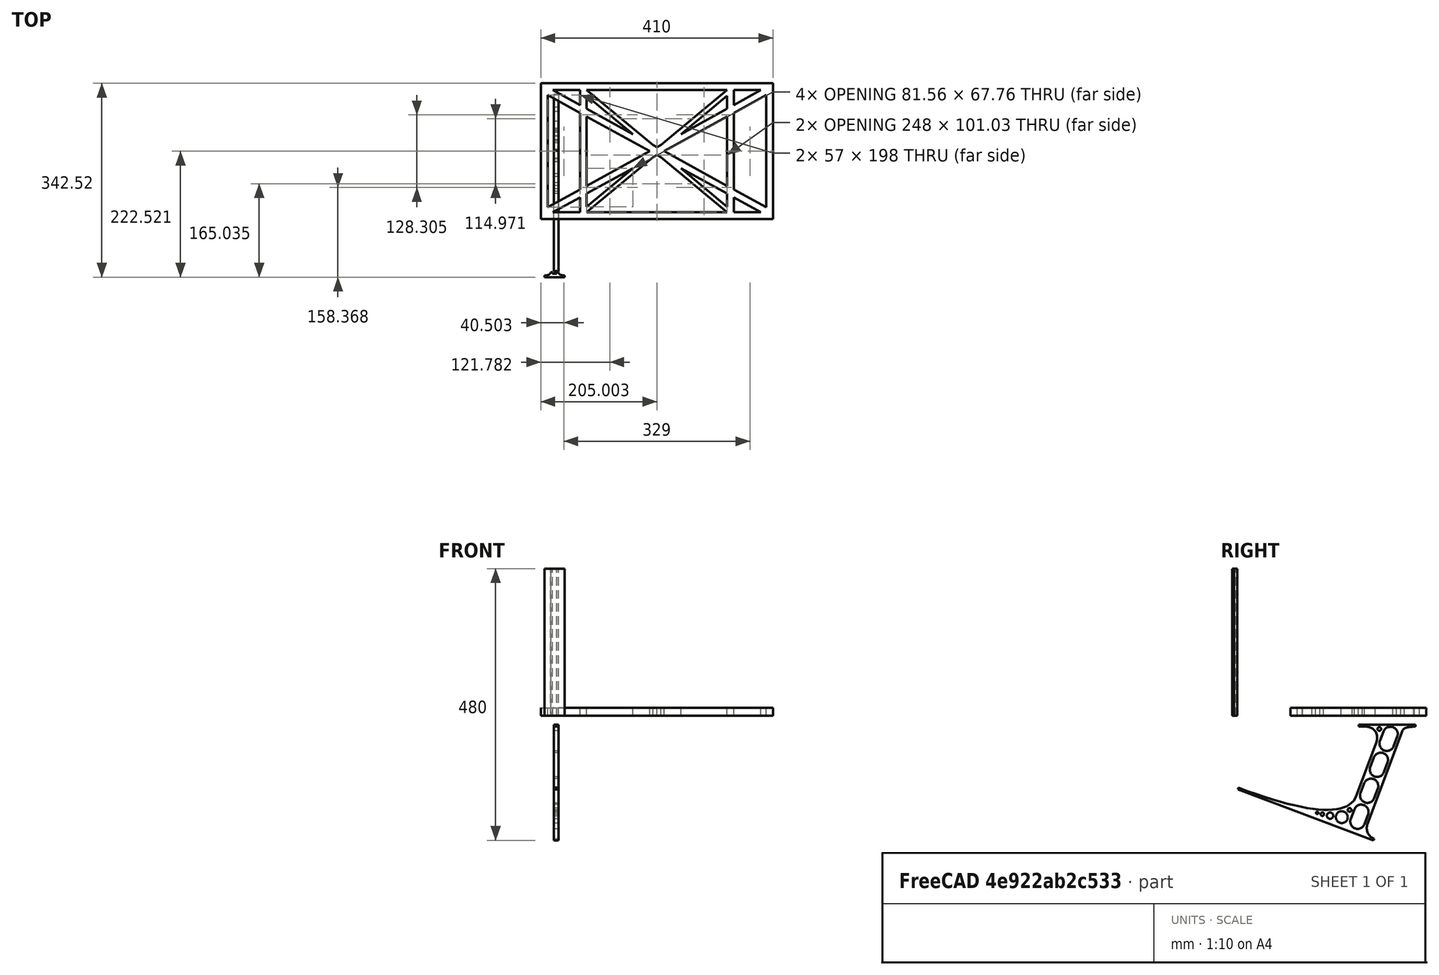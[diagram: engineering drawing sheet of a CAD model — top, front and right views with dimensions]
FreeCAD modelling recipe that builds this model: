
FCSTD DOCUMENT  (FreeCAD 0.19R0.19.2)
Label: laptopStand052
License: All rights reserved
LicenseURL: http://en.wikipedia.org/wiki/All_rights_reserved
objects: Sketcher::SketchObject×3, Part::Extrusion×3
note: 6 computed .brp shape members not serialized (recipe doc carries the construction recipe); baked Part::Feature solids carry a one-line shape summary decoded from their .brp

FEATURE [Sketcher::SketchObject] Sketch
  FullyConstrained = true
  sketch-geometry (90):
    g0: LineSegment StartX=-22.9272 StartY=136.221 StartZ=0 EndX=387.073 EndY=136.221 EndZ=0
    g1: LineSegment StartX=-22.9272 StartY=-103.779 StartZ=0 EndX=387.073 EndY=-103.779 EndZ=0
    g2: LineSegment StartX=375.073 StartY=115.221 StartZ=0 EndX=318.073 EndY=83.9235 EndZ=0
    g3: LineSegment StartX=-10.9272 StartY=-82.7794 StartZ=0 EndX=46.0728 EndY=-51.4823 EndZ=0
    g4: LineSegment StartX=-1.92719 StartY=124.221 StartZ=0 EndX=46.0728 EndY=97.8651 EndZ=0
    g5: LineSegment StartX=366.073 StartY=-91.7794 StartZ=0 EndX=318.073 EndY=-65.424 EndZ=0
    g6: LineSegment StartX=-10.9272 StartY=115.221 StartZ=0 EndX=-10.9272 EndY=-82.7794 EndZ=0
    g7: LineSegment StartX=375.073 StartY=-82.7794 StartZ=0 EndX=375.073 EndY=115.221 EndZ=0
    g8: LineSegment StartX=-1.92719 StartY=-91.7794 StartZ=0 EndX=46.0728 EndY=-91.7794 EndZ=0
    g9: LineSegment StartX=318.073 StartY=124.221 StartZ=0 EndX=366.073 EndY=124.221 EndZ=0
    g10: LineSegment StartX=306.073 StartY=-81.8102 StartZ=0 EndX=224.513 EndY=-14.0532 EndZ=0
    g11: LineSegment StartX=58.0728 StartY=114.251 StartZ=0 EndX=139.632 EndY=46.4944 EndZ=0
    g12: LineSegment StartX=306.073 StartY=124.221 StartZ=0 EndX=189.124 EndY=27.0628 EndZ=0
    g13: LineSegment StartX=58.0728 StartY=-91.7794 StartZ=0 EndX=175.022 EndY=5.37834 EndZ=0
    g14: LineSegment StartX=46.0728 StartY=124.221 StartZ=0 EndX=46.0728 EndY=97.8651 EndZ=0
    g15: LineSegment StartX=58.0728 StartY=-81.8102 StartZ=0 EndX=58.0728 EndY=-58.8351 EndZ=0
    g16: LineSegment StartX=318.073 StartY=124.221 StartZ=0 EndX=318.073 EndY=97.8651 EndZ=0
    g17: LineSegment StartX=306.073 StartY=114.251 StartZ=0 EndX=306.073 EndY=91.2763 EndZ=0
    g18: LineSegment StartX=224.513 StartY=46.4944 StartZ=0 EndX=306.073 EndY=114.251 EndZ=0
    g19: LineSegment StartX=175.022 StartY=27.0628 StartZ=0 EndX=58.0728 EndY=124.221 EndZ=0
    g20: LineSegment StartX=169.377 StartY=16.2206 StartZ=0 EndX=58.0728 EndY=77.3346 EndZ=0
    g21: LineSegment StartX=139.632 StartY=-14.0532 StartZ=0 EndX=58.0728 EndY=-81.8102 EndZ=0
    g22: LineSegment StartX=194.768 StartY=16.2206 StartZ=0 EndX=306.073 EndY=-44.8935 EndZ=0
    g23: LineSegment StartX=224.513 StartY=46.4944 StartZ=0 EndX=306.073 EndY=91.2763 EndZ=0
    g24: LineSegment StartX=139.632 StartY=-14.0532 StartZ=0 EndX=58.0728 EndY=-58.8351 EndZ=0
    g25: LineSegment StartX=189.124 StartY=5.37834 StartZ=0 EndX=306.073 EndY=-91.7794 EndZ=0
    g26: LineSegment StartX=306.073 StartY=77.3346 StartZ=0 EndX=306.073 EndY=-44.8935 EndZ=0
    g27: LineSegment StartX=318.073 StartY=83.9235 StartZ=0 EndX=318.073 EndY=-51.4823 EndZ=0
    g28: LineSegment StartX=318.073 StartY=97.8651 StartZ=0 EndX=366.073 EndY=124.221 EndZ=0
    g29: LineSegment StartX=306.073 StartY=77.3346 StartZ=0 EndX=194.768 EndY=16.2206 EndZ=0
    g30: LineSegment StartX=306.073 StartY=-58.8351 StartZ=0 EndX=224.513 EndY=-14.0532 EndZ=0
    g31: LineSegment StartX=306.073 StartY=-58.8351 StartZ=0 EndX=306.073 EndY=-81.8102 EndZ=0
    g32: LineSegment StartX=318.073 StartY=-51.4823 StartZ=0 EndX=375.073 EndY=-82.7794 EndZ=0
    g33: LineSegment StartX=318.073 StartY=-65.424 StartZ=0 EndX=318.073 EndY=-91.7794 EndZ=0
    g34: LineSegment StartX=318.073 StartY=-91.7794 StartZ=0 EndX=366.073 EndY=-91.7794 EndZ=0
    g35: LineSegment StartX=58.0728 StartY=-44.8935 StartZ=0 EndX=58.0728 EndY=77.3346 EndZ=0
    g36: LineSegment StartX=46.0728 StartY=-65.424 StartZ=0 EndX=-1.92719 EndY=-91.7794 EndZ=0
    g37: LineSegment StartX=46.0728 StartY=-65.424 StartZ=0 EndX=46.0728 EndY=-91.7794 EndZ=0
    g38: LineSegment StartX=58.0728 StartY=-44.8935 StartZ=0 EndX=169.377 EndY=16.2206 EndZ=0
    g39: LineSegment StartX=58.0728 StartY=91.2763 StartZ=0 EndX=58.0728 EndY=114.251 EndZ=0
    g40: LineSegment StartX=46.0728 StartY=83.9235 StartZ=0 EndX=46.0728 EndY=-51.4823 EndZ=0
    g41: LineSegment StartX=46.0728 StartY=124.221 StartZ=0 EndX=-1.92719 EndY=124.221 EndZ=0
    g42: LineSegment StartX=58.0728 StartY=91.2763 StartZ=0 EndX=139.632 EndY=46.4944 EndZ=0
    g43: LineSegment StartX=46.0728 StartY=83.9235 StartZ=0 EndX=-10.9272 EndY=115.221 EndZ=0
    g44: LineSegment StartX=-22.9272 StartY=136.221 StartZ=0 EndX=-42.9272 EndY=136.221 EndZ=0
    g45: LineSegment StartX=387.073 StartY=136.221 StartZ=0 EndX=407.073 EndY=136.221 EndZ=0
    g46: LineSegment StartX=-42.9272 StartY=136.221 StartZ=0 EndX=-42.9272 EndY=-103.779 EndZ=0
    g47: LineSegment StartX=-22.9272 StartY=-103.779 StartZ=0 EndX=-42.9272 EndY=-103.779 EndZ=0
    g48: LineSegment StartX=407.073 StartY=136.221 StartZ=0 EndX=407.073 EndY=-103.779 EndZ=0
    g49: LineSegment StartX=387.073 StartY=-103.779 StartZ=0 EndX=407.073 EndY=-103.779 EndZ=0
    g50: LineSegment StartX=179.022 StartY=27.0628 StartZ=0 EndX=179.022 EndY=124.221 EndZ=0
    g51: LineSegment StartX=185.124 StartY=27.0628 StartZ=0 EndX=185.124 EndY=124.221 EndZ=0
    g52: ArcOfCircle CenterX=-26.9272 CenterY=22.1087 CenterZ=0 NormalX=0 NormalY=0 NormalZ=1 AngleXU=0 Radius=8 StartAngle=1e-16 EndAngle=3.14159
    g53: ArcOfCircle CenterX=-26.9272 CenterY=-83.7794 CenterZ=0 NormalX=0 NormalY=0 NormalZ=1 AngleXU=0 Radius=8 StartAngle=3.14159 EndAngle=6.28319
    g54: LineSegment StartX=-34.9272 StartY=22.1087 StartZ=0 EndX=-34.9272 EndY=-83.7794 EndZ=0
    g55: LineSegment StartX=-18.9272 StartY=22.1087 StartZ=0 EndX=-18.9272 EndY=-83.7794 EndZ=0
    g56: LineSegment StartX=185.124 StartY=-91.7794 StartZ=0 EndX=306.073 EndY=-91.7794 EndZ=0
    g57: LineSegment StartX=179.022 StartY=-91.7794 StartZ=0 EndX=58.0728 EndY=-91.7794 EndZ=0
    g58: LineSegment StartX=306.073 StartY=124.221 StartZ=0 EndX=185.124 EndY=124.221 EndZ=0
    g59: LineSegment StartX=179.022 StartY=124.221 StartZ=0 EndX=58.0728 EndY=124.221 EndZ=0
    g60: ArcOfCircle CenterX=391.073 CenterY=22.1087 CenterZ=0 NormalX=0 NormalY=0 NormalZ=1 AngleXU=0 Radius=8 StartAngle=-4.4e-15 EndAngle=3.14159
    g61: LineSegment StartX=399.073 StartY=22.1087 StartZ=0 EndX=399.073 EndY=-83.7794 EndZ=0
    g62: LineSegment StartX=383.073 StartY=22.1087 StartZ=0 EndX=383.073 EndY=-83.7794 EndZ=0
    g63: ArcOfCircle CenterX=391.073 CenterY=-83.7794 CenterZ=0 NormalX=0 NormalY=0 NormalZ=1 AngleXU=0 Radius=8 StartAngle=3.14159 EndAngle=6.28319
    g64: Circle CenterX=175.022 CenterY=27.0628 CenterZ=0 NormalX=0 NormalY=0 NormalZ=1 AngleXU=0 Radius=1
    g65: Circle CenterX=179.022 CenterY=24.8665 CenterZ=0 NormalX=0 NormalY=0 NormalZ=1 AngleXU=0 Radius=1
    g66: Circle CenterX=179.022 CenterY=27.0628 CenterZ=0 NormalX=0 NormalY=0 NormalZ=1 AngleXU=0 Radius=1
    g67: BSplineCurve PolesCount=3 KnotsCount=2 Degree=2 IsPeriodic=0
    g68: GeomPoint X=175.022 Y=27.0628 Z=0
    g69: GeomPoint X=179.022 Y=27.0628 Z=0
    g70: Circle CenterX=189.124 CenterY=27.0628 CenterZ=0 NormalX=0 NormalY=0 NormalZ=1 AngleXU=0 Radius=1
    g71: Circle CenterX=185.124 CenterY=24.8665 CenterZ=0 NormalX=0 NormalY=0 NormalZ=1 AngleXU=0 Radius=1
    g72: Circle CenterX=185.124 CenterY=27.0628 CenterZ=0 NormalX=0 NormalY=0 NormalZ=1 AngleXU=0 Radius=1
    g73: BSplineCurve PolesCount=3 KnotsCount=2 Degree=2 IsPeriodic=0
    g74: GeomPoint X=189.124 Y=27.0628 Z=0
    g75: GeomPoint X=185.124 Y=27.0628 Z=0
    g76: Circle CenterX=175.022 CenterY=5.37834 CenterZ=0 NormalX=0 NormalY=0 NormalZ=1 AngleXU=0 Radius=1
    g77: Circle CenterX=179.022 CenterY=7.57463 CenterZ=0 NormalX=0 NormalY=0 NormalZ=1 AngleXU=0 Radius=1
    g78: Circle CenterX=179.022 CenterY=5.34704 CenterZ=0 NormalX=0 NormalY=0 NormalZ=1 AngleXU=0 Radius=1
    g79: BSplineCurve PolesCount=3 KnotsCount=2 Degree=2 IsPeriodic=0
    g80: GeomPoint X=175.022 Y=5.37834 Z=0
    g81: GeomPoint X=179.022 Y=5.34704 Z=0
    g82: Circle CenterX=189.124 CenterY=5.37834 CenterZ=0 NormalX=0 NormalY=0 NormalZ=1 AngleXU=0 Radius=1
    g83: Circle CenterX=185.124 CenterY=7.57463 CenterZ=0 NormalX=0 NormalY=0 NormalZ=1 AngleXU=0 Radius=1
    g84: Circle CenterX=185.124 CenterY=5.34704 CenterZ=0 NormalX=0 NormalY=0 NormalZ=1 AngleXU=0 Radius=1
    g85: BSplineCurve PolesCount=3 KnotsCount=2 Degree=2 IsPeriodic=0
    g86: GeomPoint X=189.124 Y=5.37834 Z=0
    g87: GeomPoint X=185.124 Y=5.34704 Z=0
    g88: LineSegment StartX=179.022 StartY=5.34704 StartZ=0 EndX=179.022 EndY=-91.7794 EndZ=0
    g89: LineSegment StartX=185.124 StartY=-91.7794 StartZ=0 EndX=185.124 EndY=5.34704 EndZ=0
  constraints (178):
    c: Horizontal(g0)
    c: Distance(g0) = 410
    c: Horizontal(g1)
    c: Block(g0)
    c: Horizontal(g8)
    c: Horizontal(g9)
    c: Tangent(g5,g20)
    c: PointOnObject(g20,g3)
    c: PointOnObject(g22,g2)
    c: Coincident(g42,g11)
    c: Coincident(g18,g23)
    c: Coincident(g24,g21)
    c: Coincident(g30,g10)
    c: Coincident(g18,g17)
    c: Tangent(g17,g26)
    c: Tangent(g16,g27)
    c: Coincident(g23,g17)
    c: Tangent(g23,g28)
    c: Coincident(g2,g27)
    c: Coincident(g29,g26)
    c: Tangent(g2,g29)
    c: Coincident(g31,g10)
    c: Tangent(g5,g30)
    c: Tangent(g26,g31)
    c: Coincident(g22,g26)
    c: Tangent(g22,g32)
    c: Coincident(g27,g32)
    c: Coincident(g33,g5)
    c: Tangent(g27,g33)
    c: Coincident(g21,g15)
    c: Tangent(g15,g35)
    c: Coincident(g24,g15)
    c: Tangent(g24,g36)
    c: Coincident(g37,g36)
    c: Tangent(g14,g37)
    c: Coincident(g3,g40)
    c: Coincident(g38,g35)
    c: Tangent(g3,g38)
    c: Tangent(g35,g39)
    c: Tangent(g14,g40)
    c: Coincident(g11,g39)
    c: Coincident(g4,g14)
    c: Coincident(g42,g39)
    c: Tangent(g4,g42)
    c: Coincident(g20,g35)
    c: Coincident(g43,g40)
    c: Tangent(g20,g43)
    c: Block(g19)
    c: Block(g12)
    c: Block(g16)
    c: Block(g28)
    c: Block(g2)
    c: Block(g32)
    c: Block(g7)
    c: Block(g30)
    c: Block(g31)
    c: Block(g5)
    c: Block(g33)
    c: Block(g18)
    c: Block(g25)
    c: Block(g13)
    c: Block(g24)
    c: Block(g21)
    c: Block(g37)
    c: Block(g36)
    c: Block(g3)
    c: Block(g6)
    c: Block(g43)
    c: Block(g4)
    c: Block(g14)
    c: Block(g11)
    c: Block(g39)
    c: Block(g29)
    c: Block(g26)
    c: Block(g20)
    c: Block(g38)
    c: Block(g41)
    c: Block(g9)
    c: Block(g34)
    c: Block(g8)
    c: Horizontal(g44)
    c: Distance(g44) = 20
    c: Coincident(g45,g0)
    c: Horizontal(g45)
    c: Distance(g45) = 20
    c: Coincident(g46,g44)
    c: Vertical(g46)
    c: Horizontal(g47)
    c: Coincident(g47,g46)
    c: Coincident(g48,g45)
    c: Vertical(g48)
    c: Coincident(g49,g1)
    c: Horizontal(g49)
    c: Coincident(g49,g48)
    c: Block(g48)
    c: Block(g47)
    c: Block(g46)
    c: Block(g1)
    c: Vertical(g50)
    c: Vertical(g51)
    c: Block(g50)
    c: Block(g51)
    c: Tangent(g52,g55) = 1.5708
    c: Tangent(g52,g54) = -1.5708
    c: Tangent(g54,g53) = -1.5708
    c: Tangent(g55,g53) = 1.5708
    c: Vertical(g54)
    c: Equal(g52,g53)
    c: Block(g55)
    c: Block(g54)
    c: Coincident(g56,g25)
    c: Horizontal(g56)
    c: Coincident(g57,g13)
    c: Horizontal(g57)
    c: Coincident(g58,g12)
    c: Coincident(g58,g51)
    c: Horizontal(g58)
    c: Coincident(g59,g50)
    c: Coincident(g59,g19)
    c: Horizontal(g59)
    c: Distance(g49) = 20
    c: Distance(g1) = 410
    c: Tangent(g60,g61) = 1.5708
    c: Tangent(g61,g63) = 1.5708
    c: Equal(g60,g63)
    c: Coincident(g62,g60)
    c: Coincident(g62,g63)
    c: Vertical(g62)
    c: Block(g61)
    c: Block(g62)
    c: Block(g22)
    c: Coincident(g67,g19)
    c: Weight(g64) = 1
    c: Equal(g64,g65)
    c: Equal(g64,g66)
    c: Coincident(g67,g50)
    c: InternalAlignment(g64,g67)
    c: InternalAlignment(g65,g67)
    c: InternalAlignment(g66,g67)
    c: InternalAlignment(g68,g67)
    c: InternalAlignment(g69,g67)
    c: Coincident(g73,g12)
    c: Weight(g70) = 1
    c: Equal(g70,g71)
    c: Equal(g70,g72)
    c: Coincident(g73,g51)
    c: InternalAlignment(g70,g73)
    c: InternalAlignment(g71,g73)
    c: InternalAlignment(g72,g73)
    c: InternalAlignment(g74,g73)
    c: InternalAlignment(g75,g73)
    c: Block(g73)
    c: Block(g67)
    c: Coincident(g79,g13)
    c: Weight(g76) = 1
    c: Equal(g76,g77)
    c: Equal(g76,g78)
    c: InternalAlignment(g76,g79)
    c: InternalAlignment(g77,g79)
    c: InternalAlignment(g78,g79)
    c: InternalAlignment(g80,g79)
    c: InternalAlignment(g81,g79)
    c: Weight(g82) = 1
    c: Equal(g82,g83)
    c: Equal(g82,g84)
    c: InternalAlignment(g82,g85)
    c: InternalAlignment(g83,g85)
    c: InternalAlignment(g84,g85)
    c: InternalAlignment(g86,g85)
    c: InternalAlignment(g87,g85)
    c: Block(g85)
    c: Block(g79)
    c: Coincident(g88,g79)
    c: Coincident(g88,g57)
    c: Vertical(g88)
    c: Coincident(g89,g56)
    c: Coincident(g89,g85)
    c: Vertical(g89)
FEATURE [Sketcher::SketchObject] Sketch001
  FullyConstrained = true
  MapMode = 4
  Placement = pos=(0,0,0) rot=(0.57735,0.57735,0.57735;2.0944rad)
  Support = -> [Sketch]
  sketch-geometry (46):
    g0: BSplineCurve PolesCount=3 KnotsCount=2 Degree=2 IsPeriodic=0
    g1: ArcOfCircle CenterX=73.122 CenterY=-32.2909 CenterZ=0 NormalX=0 NormalY=0 NormalZ=1 AngleXU=0 Radius=13 StartAngle=5.92268 EndAngle=9.06428
    g2: ArcOfCircle CenterX=66.7816 CenterY=-49.1439 CenterZ=0 NormalX=0 NormalY=0 NormalZ=1 AngleXU=0 Radius=13 StartAngle=2.78068 EndAngle=5.92131
    g3: ArcOfCircle CenterX=55.9263 CenterY=-78.1807 CenterZ=0 NormalX=0 NormalY=0 NormalZ=1 AngleXU=0 Radius=13 StartAngle=5.92268 EndAngle=9.06428
    g4: ArcOfCircle CenterX=49.5884 CenterY=-95.0342 CenterZ=0 NormalX=0 NormalY=0 NormalZ=1 AngleXU=0 Radius=13 StartAngle=2.78068 EndAngle=5.92131
    g5: ArcOfCircle CenterX=38.7206 CenterY=-124.067 CenterZ=0 NormalX=0 NormalY=0 NormalZ=1 AngleXU=0 Radius=13 StartAngle=5.92268 EndAngle=9.06428
    g6: ArcOfCircle CenterX=32.3875 CenterY=-140.92 CenterZ=0 NormalX=0 NormalY=0 NormalZ=1 AngleXU=0 Radius=13 StartAngle=2.78068 EndAngle=5.92131
    g7: ArcOfCircle CenterX=21.4715 CenterY=-169.934 CenterZ=0 NormalX=0 NormalY=0 NormalZ=1 AngleXU=0 Radius=13 StartAngle=5.92268 EndAngle=9.06428
    g8: ArcOfCircle CenterX=15.1336 CenterY=-186.787 CenterZ=0 NormalX=0 NormalY=0 NormalZ=1 AngleXU=0 Radius=13 StartAngle=2.78068 EndAngle=5.92131
    g9-g12: Circle x4 (B-spline internal-alignment scaffolding for g13; pole/knot coordinates omitted)
    g13: BSplineCurve PolesCount=4 KnotsCount=2 Degree=3 IsPeriodic=0
    g14: GeomPoint X=28.8094 Y=-19.0875 Z=0
    g15: GeomPoint X=47.0443 Y=-50.4712 Z=0
    g16: Circle CenterX=53.5586 CenterY=-23.2695 CenterZ=0 NormalX=0 NormalY=0 NormalZ=1 AngleXU=0 Radius=3.24518
    g17: Circle CenterX=-195.441 CenterY=-127.082 CenterZ=0 NormalX=0 NormalY=0 NormalZ=1 AngleXU=0 Radius=1
    g18: Circle CenterX=-8.24091 CenterY=-197.481 CenterZ=0 NormalX=0 NormalY=0 NormalZ=1 AngleXU=0 Radius=1
    g19: Circle CenterX=12.8789 CenterY=-141.321 CenterZ=0 NormalX=0 NormalY=0 NormalZ=1 AngleXU=0 Radius=1
    g20: BSplineCurve PolesCount=3 KnotsCount=2 Degree=2 IsPeriodic=0
    g21: GeomPoint X=-195.441 Y=-127.082 Z=0
    g22: GeomPoint X=12.8789 Y=-141.321 Z=0
    g23: Circle CenterX=-12.8016 CenterY=-179.036 CenterZ=0 NormalX=0 NormalY=0 NormalZ=1 AngleXU=0 Radius=10.5072
    g24: Circle CenterX=0.933922 CenterY=-166.43 CenterZ=0 NormalX=0 NormalY=0 NormalZ=1 AngleXU=0 Radius=3.26661
    g25: Circle CenterX=-33.5518 CenterY=-176.44 CenterZ=0 NormalX=0 NormalY=0 NormalZ=1 AngleXU=0 Radius=5.64388
    g26: Circle CenterX=-47.2366 CenterY=-173.859 CenterZ=0 NormalX=0 NormalY=0 NormalZ=1 AngleXU=0 Radius=3.01653
    g27: Circle CenterX=-56.2595 CenterY=-171.456 CenterZ=0 NormalX=0 NormalY=0 NormalZ=1 AngleXU=0 Radius=2.12826
    g28: ArcOfCircle CenterX=51.2151 CenterY=-198.473 CenterZ=0 NormalX=0 NormalY=0 NormalZ=1 AngleXU=0 Radius=20 StartAngle=2.78189 EndAngle=4.35269
    g29: LineSegment StartX=32.4951 StartY=-191.433 StartZ=0 EndX=94.6577 EndY=-26.1351 EndZ=0
    g30: LineSegment StartX=43.1192 StartY=-220.001 StartZ=0 EndX=-196.497 EndY=-129.89 EndZ=0
    g31: LineSegment StartX=43.1192 StartY=-220.001 StartZ=0 EndX=44.1752 EndY=-217.193 EndZ=0
    g32: LineSegment StartX=117.223 StartY=-19.0875 StartZ=0 EndX=117.223 EndY=-16.0875 EndZ=0
    g33: LineSegment StartX=117.223 StartY=-16.0875 StartZ=0 EndX=17.2232 EndY=-16.0875 EndZ=0
    g34: LineSegment StartX=17.2232 StartY=-16.0875 StartZ=0 EndX=17.2232 EndY=-19.0875 EndZ=0
    g35: LineSegment StartX=28.8094 StartY=-19.0875 StartZ=0 EndX=17.2232 EndY=-19.0875 EndZ=0
    g36: LineSegment StartX=47.0443 StartY=-50.4712 StartZ=0 EndX=12.8789 EndY=-141.321 EndZ=0
    g37: LineSegment StartX=-195.441 StartY=-127.082 StartZ=0 EndX=-196.497 EndY=-129.89 EndZ=0
    g38: LineSegment StartX=85.2864 StartY=-36.8765 StartZ=0 EndX=78.9396 EndY=-53.7463 EndZ=0
    g39: LineSegment StartX=60.9577 StartY=-27.7052 StartZ=0 EndX=54.6191 EndY=-44.5532 EndZ=0
    g40: LineSegment StartX=68.0907 StartY=-82.7664 StartZ=0 EndX=61.7465 EndY=-99.6365 EndZ=0
    g41: LineSegment StartX=43.7619 StartY=-73.595 StartZ=0 EndX=37.426 EndY=-90.4435 EndZ=0
    g42: LineSegment StartX=50.885 StartY=-128.652 StartZ=0 EndX=44.5456 EndY=-145.522 EndZ=0
    g43: LineSegment StartX=26.5562 StartY=-119.481 StartZ=0 EndX=20.2251 EndY=-136.329 EndZ=0
    g44: LineSegment StartX=9.3071 StartY=-165.349 StartZ=0 EndX=2.97115 EndY=-182.197 EndZ=0
    g45: LineSegment StartX=33.6358 StartY=-174.52 StartZ=0 EndX=27.2917 EndY=-191.39 EndZ=0
  constraints (70):
    c: Block(g0)
    c: Block(g1)
    c: Block(g2)
    c: Block(g4)
    c: Block(g3)
    c: Block(g6)
    c: Block(g5)
    c: Block(g8)
    c: Block(g7)
    c: Weight(g9) = 1
    c: Equal(g9,g10)
    c: Equal(g9,g11)
    c: Equal(g9,g12)
    c: InternalAlignment(g9-g12 -> g13) x4
    c: InternalAlignment(g14,g13)
    c: InternalAlignment(g15,g13)
    c: Block(g16)
    c: Weight(g17) = 1
    c: Equal(g17,g18)
    c: Equal(g17,g19)
    c: InternalAlignment(g17,g20)
    c: InternalAlignment(g18,g20)
    c: InternalAlignment(g19,g20)
    c: InternalAlignment(g21,g20)
    c: InternalAlignment(g22,g20)
    c: Block(g20)
    c: Block(g23)
    c: Block(g24)
    c: Block(g25)
    c: Block(g26)
    c: Block(g27)
    c: Block(g28)
    c: Coincident(g29,g28)
    c: Coincident(g29,g0)
    c: Block(g13)
    c: Coincident(g31,g30)
    c: Coincident(g31,g28)
    c: Block(g31)
    c: Coincident(g32,g0)
    c: Vertical(g32)
    c: Coincident(g33,g32)
    c: Horizontal(g33)
    c: Coincident(g34,g33)
    c: Vertical(g34)
    c: Block(g33)
    c: Coincident(g35,g13)
    c: Coincident(g35,g34)
    c: Horizontal(g35)
    c: Coincident(g36,g13)
    c: Coincident(g36,g20)
    c: Coincident(g37,g20)
    c: Coincident(g37,g30)
    c: Block(g30)
    c: Coincident(g38,g1)
    c: Coincident(g38,g2)
    c: Coincident(g39,g1)
    c: Coincident(g39,g2)
    c: Coincident(g40,g3)
    c: Coincident(g40,g4)
    c: Coincident(g41,g3)
    c: Coincident(g41,g4)
    c: Coincident(g42,g5)
    c: Coincident(g42,g6)
    c: Coincident(g43,g5)
    c: Coincident(g43,g6)
    c: Coincident(g44,g7)
    c: Coincident(g44,g8)
    c: Coincident(g45,g7)
    c: Coincident(g45,g8)
    c: Distance(g30) = 256
FEATURE [Part::Extrusion] Extrude002
  Base = -> Sketch001
  Dir = (1,0,0)
  DirMode = 2
  FaceMakerClass = Part::FaceMakerBullseye
  LengthFwd = 8
  LengthRev = 0
  Solid = true
  Symmetric = false
FEATURE [Sketcher::SketchObject] Sketch002
  FullyConstrained = true
  sketch-geometry (20):
    g0: LineSegment StartX=-2.77179 StartY=-200.304 StartZ=0 EndX=5.22821 EndY=-200.304 EndZ=0
    g1: LineSegment StartX=5.22821 StartY=-200.304 StartZ=0 EndX=5.22821 EndY=-197.304 EndZ=0
    g2: LineSegment StartX=-2.77179 StartY=-200.304 StartZ=0 EndX=-2.77179 EndY=-197.304 EndZ=0
    g3: LineSegment StartX=5.22821 StartY=-197.304 StartZ=0 EndX=8.22821 EndY=-197.304 EndZ=0
    g4: LineSegment StartX=-2.77179 StartY=-197.304 StartZ=0 EndX=-5.77179 EndY=-197.304 EndZ=0
    g5: LineSegment StartX=19.2282 StartY=-203.304 StartZ=0 EndX=19.2282 EndY=-206.304 EndZ=0
    g6: LineSegment StartX=-16.7718 StartY=-203.304 StartZ=0 EndX=-16.7718 EndY=-206.304 EndZ=0
    g7: LineSegment StartX=-16.7718 StartY=-206.304 StartZ=0 EndX=19.2282 EndY=-206.304 EndZ=0
    g8: Circle CenterX=-16.7718 CenterY=-203.304 CenterZ=0 NormalX=0 NormalY=0 NormalZ=1 AngleXU=0 Radius=1
    g9: Circle CenterX=-5.77179 CenterY=-203.304 CenterZ=0 NormalX=0 NormalY=0 NormalZ=1 AngleXU=0 Radius=1
    g10: Circle CenterX=-5.77179 CenterY=-197.304 CenterZ=0 NormalX=0 NormalY=0 NormalZ=1 AngleXU=0 Radius=1
    g11: BSplineCurve PolesCount=3 KnotsCount=2 Degree=2 IsPeriodic=0
    g12: GeomPoint X=-16.7718 Y=-203.304 Z=0
    g13: GeomPoint X=-5.77179 Y=-197.304 Z=0
    g14: Circle CenterX=19.2282 CenterY=-203.304 CenterZ=0 NormalX=0 NormalY=0 NormalZ=1 AngleXU=0 Radius=1
    g15: Circle CenterX=8.22821 CenterY=-203.304 CenterZ=0 NormalX=0 NormalY=0 NormalZ=1 AngleXU=0 Radius=1
    g16: Circle CenterX=8.22821 CenterY=-197.304 CenterZ=0 NormalX=0 NormalY=0 NormalZ=1 AngleXU=0 Radius=1
    g17: BSplineCurve PolesCount=3 KnotsCount=2 Degree=2 IsPeriodic=0
    g18: GeomPoint X=19.2282 Y=-203.304 Z=0
    g19: GeomPoint X=8.22821 Y=-197.304 Z=0
  constraints (41):
    c: Horizontal(g0)
    c: Distance(g0) = 8
    c: Coincident(g1,g0)
    c: Vertical(g1)
    c: Distance(g1) = 3
    c: Coincident(g2,g0)
    c: Vertical(g2)
    c: Distance(g2) = 3
    c: Coincident(g3,g1)
    c: Horizontal(g3)
    c: Distance(g3) = 3
    c: Coincident(g4,g2)
    c: Horizontal(g4)
    c: Distance(g4) = 3
    c: Vertical(g5)
    c: Vertical(g6)
    c: Coincident(g7,g6)
    c: Coincident(g7,g5)
    c: Weight(g8) = 1
    c: Equal(g8,g9)
    c: Equal(g8,g10)
    c: Coincident(g11,g4)
    c: InternalAlignment(g8,g11)
    c: InternalAlignment(g9,g11)
    c: InternalAlignment(g10,g11)
    c: InternalAlignment(g12,g11)
    c: InternalAlignment(g13,g11)
    c: Coincident(g17,g5)
    c: Weight(g14) = 1
    c: Equal(g14,g15)
    c: Equal(g14,g16)
    c: Coincident(g17,g3)
    c: InternalAlignment(g14,g17)
    c: InternalAlignment(g15,g17)
    c: InternalAlignment(g16,g17)
    c: InternalAlignment(g18,g17)
    c: InternalAlignment(g19,g17)
    c: Block(g7)
    c: Block(g17)
    c: Block(g11)
    c: Block(g6)
FEATURE [Part::Extrusion] Extrude003
  Base = -> Sketch002
  Dir = (0,0,1)
  DirMode = 2
  FaceMakerClass = Part::FaceMakerBullseye
  LengthFwd = 260
  LengthRev = 0
  Solid = true
  Symmetric = false
FEATURE [Part::Extrusion] Extrude
  Base = -> Sketch
  Dir = (0,0,1)
  DirMode = 2
  FaceMakerClass = Part::FaceMakerBullseye
  LengthFwd = 14
  LengthRev = 0
  Solid = true
  Symmetric = false
